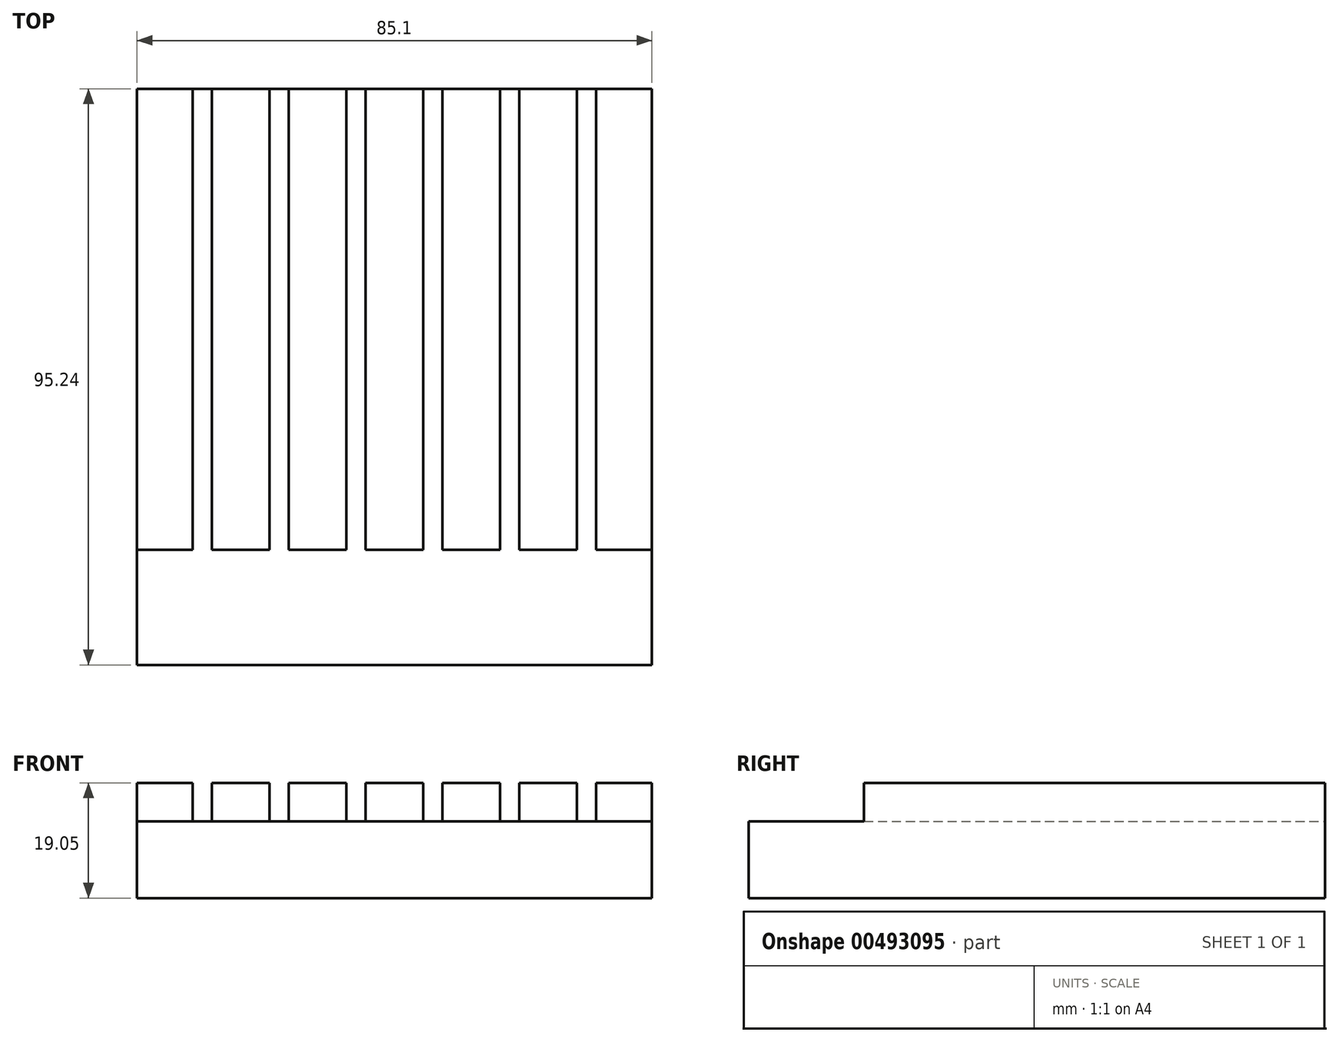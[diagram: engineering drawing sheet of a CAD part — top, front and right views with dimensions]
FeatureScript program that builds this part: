
annotation { "Feature Type Name" : "Feature", "Feature Type Description" : "" }
export const myFeature = defineFeature(function(context is Context, id is Id, definition is map)
    precondition{}
    {
        {
            var Q0;
            Q0=qCreatedBy(makeId("Top.planeOp"),FACE);
            var sketch = newSketch(context, id + "F0", { "sketchPlane" : qUnion([Q0])});
            skLineSegment(sketch, "E0.bottom", {"start": v(-42.55, 47.63) * mm, "end": v(42.55, 47.63) * mm});
            skLineSegment(sketch, "E0.top", {"start": v(-42.55, -47.63) * mm, "end": v(42.55, -47.63) * mm});
            skLineSegment(sketch, "E0.left", {"start": v(-42.55, 47.63) * mm, "end": v(-42.55, -47.63) * mm});
            skLineSegment(sketch, "E0.right", {"start": v(42.55, 47.63) * mm, "end": v(42.55, -47.63) * mm});
            skPoint(sketch, "E0.middle", {"position": v(0, 0) * mm});
            skSolve(sketch);
        }
        {
            var Q0;
            Q0=qSketchRegion(id+"F0",true);
            extrude(context, id + "F1", {"entities" : qUnion([Q0]), "depth" : 19.05 * mm});
        }
        {
            var Q0;
            Q0=makeQuery(id+"F1.opExtrude","CAP_FACE",FACE,{"disambiguationData":[OSD([sQuery(id+"F0.wireOp",EDGE,"E0.bottom"),sQuery(id+"F0.wireOp",EDGE,"E0.top"),sQuery(id+"F0.wireOp",EDGE,"E0.left"),sQuery(id+"F0.wireOp",EDGE,"E0.right")])],"isStart":false});
            var sketch = newSketch(context, id + "F2", { "sketchPlane" : qUnion([Q0])});
            skLineSegment(sketch, "E1.bottom", {"start": v(-33.34, -50.8) * mm, "end": v(-30.16, -50.8) * mm});
            skLineSegment(sketch, "E1.top", {"start": v(-33.34, 50.8) * mm, "end": v(-30.16, 50.8) * mm});
            skLineSegment(sketch, "E1.left", {"start": v(-33.34, -50.8) * mm, "end": v(-33.34, 50.8) * mm});
            skLineSegment(sketch, "E1.right", {"start": v(-30.16, -50.8) * mm, "end": v(-30.16, 50.8) * mm});
            skLineSegment(sketch, "E2", {"start": v(-59.48, 0) * mm, "end": v(76.02, 0) * mm, "construction": true});
            skLineSegment(sketch, "E3.1.0.0", {"start": v(-17.46, -50.8) * mm, "end": v(-17.46, 50.8) * mm});
            skLineSegment(sketch, "E3.1.0.1", {"start": v(-20.64, -50.8) * mm, "end": v(-20.64, 50.8) * mm});
            skLineSegment(sketch, "E3.1.0.2", {"start": v(-20.64, -50.8) * mm, "end": v(-17.46, -50.8) * mm});
            skLineSegment(sketch, "E3.1.0.3", {"start": v(-20.64, 50.8) * mm, "end": v(-17.46, 50.8) * mm});
            skLineSegment(sketch, "E3.2.0.0", {"start": v(-4.76, -50.8) * mm, "end": v(-4.76, 50.8) * mm});
            skLineSegment(sketch, "E3.2.0.1", {"start": v(-7.94, -50.8) * mm, "end": v(-7.94, 50.8) * mm});
            skLineSegment(sketch, "E3.2.0.2", {"start": v(-7.94, -50.8) * mm, "end": v(-4.76, -50.8) * mm});
            skLineSegment(sketch, "E3.2.0.3", {"start": v(-7.94, 50.8) * mm, "end": v(-4.76, 50.8) * mm});
            skLineSegment(sketch, "E3.3.0.0", {"start": v(7.94, -50.8) * mm, "end": v(7.94, 50.8) * mm});
            skLineSegment(sketch, "E3.3.0.1", {"start": v(4.76, -50.8) * mm, "end": v(4.76, 50.8) * mm});
            skLineSegment(sketch, "E3.3.0.2", {"start": v(4.76, -50.8) * mm, "end": v(7.94, -50.8) * mm});
            skLineSegment(sketch, "E3.3.0.3", {"start": v(4.76, 50.8) * mm, "end": v(7.94, 50.8) * mm});
            skLineSegment(sketch, "E3.4.0.0", {"start": v(20.64, -50.8) * mm, "end": v(20.64, 50.8) * mm});
            skLineSegment(sketch, "E3.4.0.1", {"start": v(17.46, -50.8) * mm, "end": v(17.46, 50.8) * mm});
            skLineSegment(sketch, "E3.4.0.2", {"start": v(17.46, -50.8) * mm, "end": v(20.64, -50.8) * mm});
            skLineSegment(sketch, "E3.4.0.3", {"start": v(17.46, 50.8) * mm, "end": v(20.64, 50.8) * mm});
            skLineSegment(sketch, "E3.5.0.0", {"start": v(33.34, -50.8) * mm, "end": v(33.34, 50.8) * mm});
            skLineSegment(sketch, "E3.5.0.1", {"start": v(30.16, -50.8) * mm, "end": v(30.16, 50.8) * mm});
            skLineSegment(sketch, "E3.5.0.2", {"start": v(30.16, -50.8) * mm, "end": v(33.34, -50.8) * mm});
            skLineSegment(sketch, "E3.5.0.3", {"start": v(30.16, 50.8) * mm, "end": v(33.34, 50.8) * mm});
            skLineSegment(sketch, "E3.direction1", {"start": v(-33.34, -50.8) * mm, "end": v(-20.64, -50.8) * mm, "construction": true});
            skLineSegment(sketch, "E4", {"start": v(0, 68.28) * mm, "end": v(0, -69.42) * mm, "construction": true});
            skSolve(sketch);
        }
        {
            var Q0;
            Q0 = qSketchRegion(id + "F2", true);
            extrude(context, id + "F3", {"entities" : qUnion([Q0]), "operationType" : NewBodyOperationType.REMOVE, "oppositeDirection" : true, "depth" : 6.35 * mm});
        }
        {
            var Q0;
            Q0=makeQuery(id+"F1.opExtrude","SWEPT_FACE",FACE,{"disambiguationData":[OSD([sQuery(id+"F0.wireOp",EDGE,"E0.right")])]});
            var sketch = newSketch(context, id + "F4", { "sketchPlane" : qUnion([Q0])});
            skLineSegment(sketch, "E5.bottom", {"start": v(-47.62, 19.05) * mm, "end": v(-28.57, 19.05) * mm});
            skLineSegment(sketch, "E5.top", {"start": v(-47.62, 12.7) * mm, "end": v(-28.57, 12.7) * mm});
            skLineSegment(sketch, "E5.left", {"start": v(-47.62, 19.05) * mm, "end": v(-47.62, 12.7) * mm});
            skLineSegment(sketch, "E5.right", {"start": v(-28.57, 19.05) * mm, "end": v(-28.57, 12.7) * mm});
            skSolve(sketch);
        }
        {
            var Q0;
            Q0 = qSketchRegion(id + "F4", true);
            extrude(context, id + "F5", {"entities" : qUnion([Q0]), "operationType" : NewBodyOperationType.REMOVE, "endBound" : BoundingType.THROUGH_ALL, "oppositeDirection" : true, "depth" : 25.4 * mm});
        }
    });
